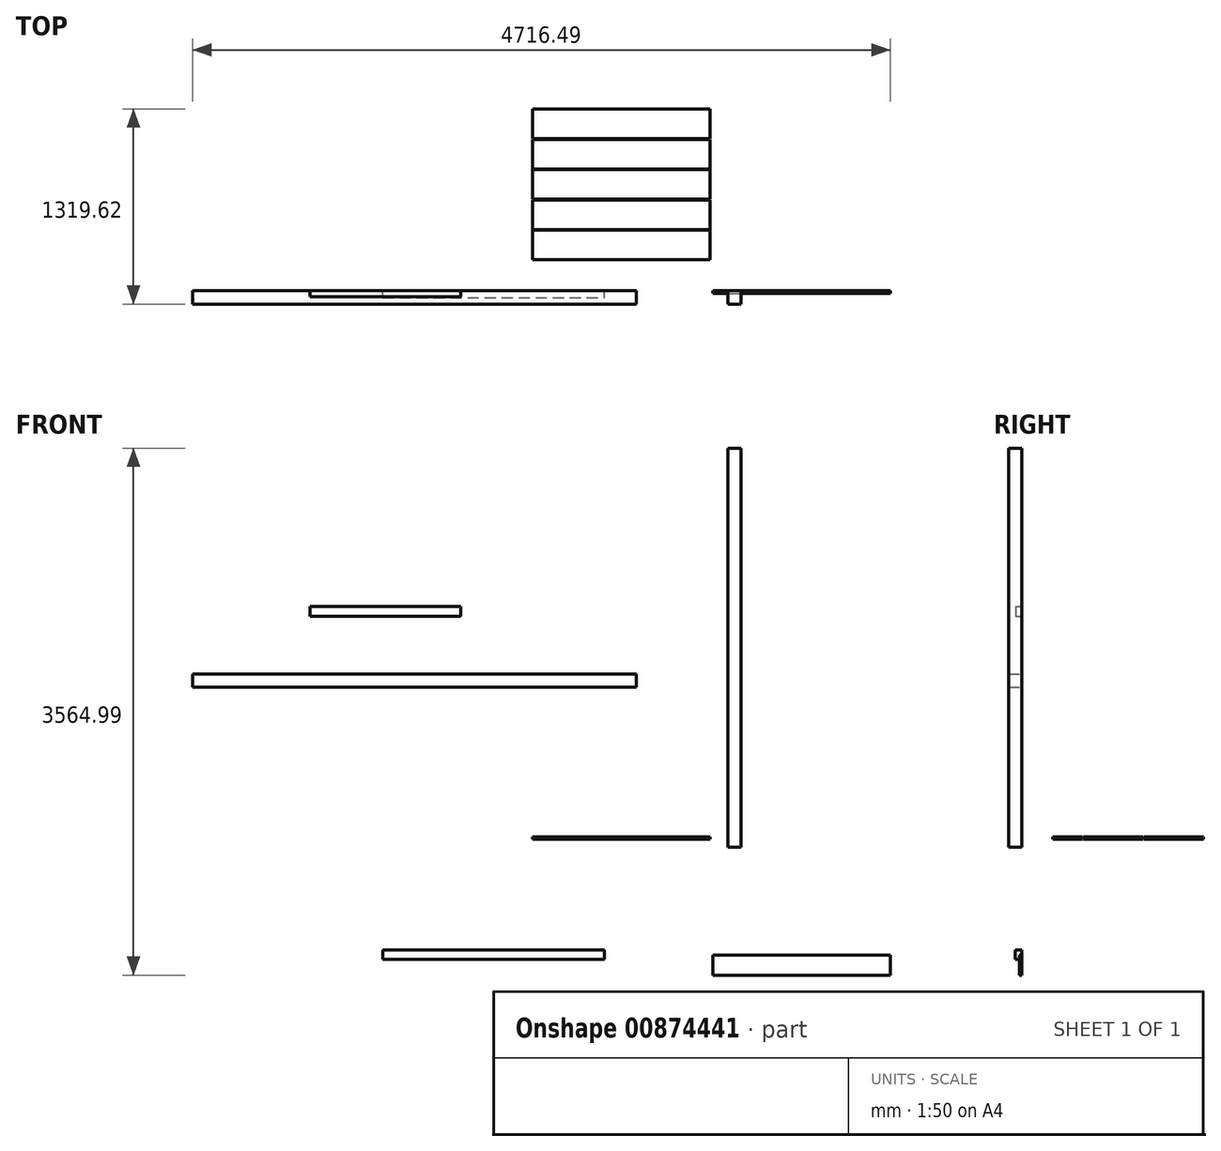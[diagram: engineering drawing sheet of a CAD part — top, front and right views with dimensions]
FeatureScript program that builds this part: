
annotation { "Feature Type Name" : "Feature", "Feature Type Description" : "" }
export const myFeature = defineFeature(function(context is Context, id is Id, definition is map)
    precondition{}
    {
        {
            var Q0;
            Q0=qCreatedBy(makeId("Front.planeOp"),FACE);
            var sketch = newSketch(context, id + "F0", { "sketchPlane" : qUnion([Q0])});
            skLineSegment(sketch, "E0.bottom", {"start": v(-138.11, 2646.7) * mm, "end": v(-48.11, 2646.7) * mm});
            skLineSegment(sketch, "E0.top", {"start": v(-138.11, -53.3) * mm, "end": v(-48.11, -53.3) * mm});
            skLineSegment(sketch, "E0.left", {"start": v(-138.11, 2646.7) * mm, "end": v(-138.11, -53.3) * mm});
            skLineSegment(sketch, "E0.right", {"start": v(-48.11, 2646.7) * mm, "end": v(-48.11, -53.3) * mm});
            skSolve(sketch);
        }
        {
            var Q0;
            Q0 = qSketchRegion(id + "F0", true);
            extrude(context, id + "F1", {"entities" : qUnion([Q0]), "depth" : 90 * mm, "offsetDistance" : 25 * mm});
        }
        {
            var Q0;
            Q0=qCreatedBy(makeId("Front.planeOp"),FACE);
            var sketch = newSketch(context, id + "F2", { "sketchPlane" : qUnion([Q0])});
            skLineSegment(sketch, "E1.bottom", {"start": v(-3757.28, 1119.11) * mm, "end": v(-757.28, 1119.11) * mm});
            skLineSegment(sketch, "E1.top", {"start": v(-3757.28, 1029.11) * mm, "end": v(-757.28, 1029.11) * mm});
            skLineSegment(sketch, "E1.left", {"start": v(-3757.28, 1119.11) * mm, "end": v(-3757.28, 1029.11) * mm});
            skLineSegment(sketch, "E1.right", {"start": v(-757.28, 1119.11) * mm, "end": v(-757.28, 1029.11) * mm});
            skSolve(sketch);
        }
        {
            var Q0;
            Q0 = qSketchRegion(id + "F2", true);
            extrude(context, id + "F3", {"entities" : qUnion([Q0]), "depth" : 90 * mm, "offsetDistance" : 25 * mm});
        }
        {
            var Q0;
            Q0=qCreatedBy(makeId("Front.planeOp"),FACE);
            var sketch = newSketch(context, id + "F4", { "sketchPlane" : qUnion([Q0])});
            skLineSegment(sketch, "E2.bottom", {"start": v(-2472.71, -746.53) * mm, "end": v(-972.71, -746.53) * mm});
            skLineSegment(sketch, "E2.top", {"start": v(-2472.71, -811.53) * mm, "end": v(-972.71, -811.53) * mm});
            skLineSegment(sketch, "E2.left", {"start": v(-2472.71, -746.53) * mm, "end": v(-2472.71, -811.53) * mm});
            skLineSegment(sketch, "E2.right", {"start": v(-972.71, -746.53) * mm, "end": v(-972.71, -811.53) * mm});
            skSolve(sketch);
        }
        {
            var Q0;
            Q0 = qSketchRegion(id + "F4", true);
            extrude(context, id + "F5", {"entities" : qUnion([Q0]), "depth" : 45 * mm, "offsetDistance" : 25 * mm});
        }
        {
            var Q0;
            Q0=qCreatedBy(makeId("Front.planeOp"),FACE);
            var sketch = newSketch(context, id + "F6", { "sketchPlane" : qUnion([Q0])});
            skLineSegment(sketch, "E3.bottom", {"start": v(-240.79, -783.29) * mm, "end": v(959.21, -783.29) * mm});
            skLineSegment(sketch, "E3.top", {"start": v(-240.79, -918.29) * mm, "end": v(959.21, -918.29) * mm});
            skLineSegment(sketch, "E3.left", {"start": v(-240.79, -783.29) * mm, "end": v(-240.79, -918.29) * mm});
            skLineSegment(sketch, "E3.right", {"start": v(959.21, -783.29) * mm, "end": v(959.21, -918.29) * mm});
            skSolve(sketch);
        }
        {
            var Q0;
            Q0=makeQuery(id+"F6.imprint","IMPRINT",FACE,{"disambiguationData":[TD([[makeQuery(id+"F6.imprint","IMPRINT",EDGE,{"derivedFrom":sQuery(id+"F6.wireOp",EDGE,"E3.bottom")}),-1.0]])]});
            extrude(context, id + "F7", {"entities" : qUnion([Q0]), "depth" : 17 * mm, "offsetDistance" : 25 * mm});
        }
        {
            var Q0;
            Q0=qCreatedBy(makeId("Front.planeOp"),FACE);
            var sketch = newSketch(context, id + "F8", { "sketchPlane" : qUnion([Q0])});
            skLineSegment(sketch, "E4.bottom", {"start": v(-2965.11, 1574.98) * mm, "end": v(-1945.11, 1574.98) * mm});
            skLineSegment(sketch, "E4.top", {"start": v(-2965.11, 1509.98) * mm, "end": v(-1945.11, 1509.98) * mm});
            skLineSegment(sketch, "E4.left", {"start": v(-2965.11, 1574.98) * mm, "end": v(-2965.11, 1509.98) * mm});
            skLineSegment(sketch, "E4.right", {"start": v(-1945.11, 1574.98) * mm, "end": v(-1945.11, 1509.98) * mm});
            skSolve(sketch);
        }
        {
            var Q0;
            Q0=makeQuery(id+"F8.imprint","IMPRINT",FACE,{"disambiguationData":[TD([[makeQuery(id+"F8.imprint","IMPRINT",EDGE,{"derivedFrom":sQuery(id+"F8.wireOp",EDGE,"E4.bottom")}),-1.0]])]});
            extrude(context, id + "F9", {"entities" : qUnion([Q0]), "depth" : 40 * mm, "offsetDistance" : 25 * mm});
        }
        {
            var Q0;
            Q0=qCreatedBy(makeId("Top.planeOp"),FACE);
            var sketch = newSketch(context, id + "F10", { "sketchPlane" : qUnion([Q0])});
            skLineSegment(sketch, "E5.bottom", {"start": v(-1460.4, 1229.62) * mm, "end": v(-260.4, 1229.62) * mm});
            skLineSegment(sketch, "E5.top", {"start": v(-1460.4, 209.62) * mm, "end": v(-260.4, 209.62) * mm});
            skLineSegment(sketch, "E5.left", {"start": v(-1460.4, 1229.62) * mm, "end": v(-1460.4, 1029.62) * mm});
            skLineSegment(sketch, "E5.right", {"start": v(-260.4, 1229.62) * mm, "end": v(-260.4, 1029.62) * mm});
            skLineSegment(sketch, "E6", {"start": v(-1460.4, 1029.62) * mm, "end": v(-260.4, 1029.62) * mm});
            skLineSegment(sketch, "E7", {"start": v(-260.4, 1024.62) * mm, "end": v(-1460.4, 1024.62) * mm});
            skLineSegment(sketch, "E8", {"start": v(-1460.4, 1024.62) * mm, "end": v(-1460.4, 824.62) * mm});
            skLineSegment(sketch, "E9", {"start": v(-1460.4, 824.62) * mm, "end": v(-260.4, 824.62) * mm});
            skLineSegment(sketch, "E10", {"start": v(-260.4, 819.62) * mm, "end": v(-1460.4, 819.62) * mm});
            skLineSegment(sketch, "E11", {"start": v(-1460.4, 819.62) * mm, "end": v(-1460.4, 619.62) * mm});
            skLineSegment(sketch, "E12", {"start": v(-1460.4, 619.62) * mm, "end": v(-260.4, 619.62) * mm});
            skLineSegment(sketch, "E13", {"start": v(-260.4, 614.62) * mm, "end": v(-1460.4, 614.62) * mm});
            skLineSegment(sketch, "E14", {"start": v(-1460.4, 614.62) * mm, "end": v(-1460.4, 414.62) * mm});
            skLineSegment(sketch, "E15", {"start": v(-1460.4, 414.62) * mm, "end": v(-260.4, 414.62) * mm});
            skLineSegment(sketch, "E16", {"start": v(-260.4, 409.62) * mm, "end": v(-1460.4, 409.62) * mm});
            skLineSegment(sketch, "E17.trimOffspring", {"start": v(-260.4, 819.62) * mm, "end": v(-260.4, 619.62) * mm});
            skLineSegment(sketch, "E18.trimOffspring", {"start": v(-260.4, 614.62) * mm, "end": v(-260.4, 414.62) * mm});
            skLineSegment(sketch, "E19.trimOffspring", {"start": v(-260.4, 409.62) * mm, "end": v(-260.4, 209.62) * mm});
            skLineSegment(sketch, "E20.trimOffspring", {"start": v(-1460.4, 409.62) * mm, "end": v(-1460.4, 209.62) * mm});
            skLineSegment(sketch, "E21.trimOffspring", {"start": v(-260.4, 1024.62) * mm, "end": v(-260.4, 824.62) * mm});
            skSolve(sketch);
        }
        {
            var Q0;
            Q0=makeQuery(id+"F10.imprint","IMPRINT",FACE,{"disambiguationData":[TD([[makeQuery(id+"F10.imprint","IMPRINT",EDGE,{"derivedFrom":sQuery(id+"F10.wireOp",EDGE,"E7")}),1.0]])]});
            var Q1;
            Q1=makeQuery(id+"F10.imprint","IMPRINT",FACE,{"disambiguationData":[TD([[makeQuery(id+"F10.imprint","IMPRINT",EDGE,{"derivedFrom":sQuery(id+"F10.wireOp",EDGE,"E5.bottom")}),-1.0]])]});
            var Q2;
            Q2=makeQuery(id+"F10.imprint","IMPRINT",FACE,{"disambiguationData":[TD([[makeQuery(id+"F10.imprint","IMPRINT",EDGE,{"derivedFrom":sQuery(id+"F10.wireOp",EDGE,"E10")}),1.0]])]});
            var Q3;
            Q3=makeQuery(id+"F10.imprint","IMPRINT",FACE,{"disambiguationData":[TD([[makeQuery(id+"F10.imprint","IMPRINT",EDGE,{"derivedFrom":sQuery(id+"F10.wireOp",EDGE,"E13")}),1.0]])]});
            var Q4;
            Q4=makeQuery(id+"F10.imprint","IMPRINT",FACE,{"disambiguationData":[TD([[makeQuery(id+"F10.imprint","IMPRINT",EDGE,{"derivedFrom":sQuery(id+"F10.wireOp",EDGE,"E5.top")}),1.0]])]});
            extrude(context, id + "F11", {"entities" : qUnion([Q0, Q1, Q2, Q3, Q4]), "depth" : 17 * mm, "offsetDistance" : 25 * mm});
        }
    });
